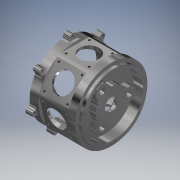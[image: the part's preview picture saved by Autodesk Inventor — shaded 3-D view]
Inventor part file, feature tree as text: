
AUTODESK INVENTOR PART (.ipt)
format: ipt  version: 2018 (Build 220112000, 112)  size: 513,024 bytes
history: native  units: mm
features: sketch x10, extrude x10, hole x4, pattern_circular x2, direct_edit x1, chamfer x1, other x1, revolve x1, projected_geometry x1
ambient origin geometry x8: Origin, YZ Plane, XZ Plane, XY Plane, X Axis, Y Axis, Z Axis, Center Point
bodies: Solid1 (feature_tree)
feature tree (31):
  sketch  "Sketch1"  dims[d0=100.0mm d1=90.0mm]
  extrude  "Extrusion1"  Depth=90.0mm
  extrude  "Extrusion2"  Depth=67.0mm TaperAngle=0.0deg
  extrude  "Extrusion3"  Depth=4.07mm
  extrude  "Extrusion4"  Depth=13.0mm TaperAngle=0.0deg
  extrude  "Extrusion5"  Depth=18.0mm
  direct_edit  "Direct Edit1"
  extrude  "Extrusion6"  Depth=12.0mm
  extrude  "Extrusion7"  Depth=30.0mm TaperAngle=360.0deg
  chamfer  "Chamfer1"  Distance=9.0mm
  extrude  "Extrusion8"  Depth=10.0mm
  sketch  "Sketch8"  dims[d28=8.0mm d29=30.0mm d31=360.0deg]
  extrude  "Extrusion9"  Depth=10.0mm TaperAngle=0.0deg
  hole  "Hole1"  [1 undecoded]
  extrude  "Extrusion10"  Depth=10.0mm TaperAngle=0.0deg
  hole  "Hole2"  [1 undecoded]
  hole  "Hole3"  [1 undecoded]
  other  "Work Axis1"
  pattern_circular  "Circular Pattern1"  [2 undecoded]
  hole  "Hole4"  [1 undecoded]
  pattern_circular  "Circular Pattern2"  [2 undecoded]
  sketch  "Sketch2"  dims[d2=80.0mm d3=67.0mm d4=0.0mm]
  sketch  "Sketch4"  dims[d5=4.07mm d6=0.0mm d7=85.0mm]
  sketch  "Sketch5"  dims[d8=50.0mm d9=0.0mm d10=13.0mm d11=0.0mm]
  sketch  "Sketch6"  dims[d12=43.0mm d22=21.5mm d25=18.0mm]
  sketch  "Sketch7"  dims[d26=25.0mm d27=12.0mm]
  sketch  "Sketch9"  dims[d33=21.5mm]
  sketch  "Sketch10"  dims[d34=21.5mm d35=9.0mm d36=0.0mm]
  sketch  "Sketch11"  dims[d37=-15.707963mm d38=35.0mm d39=10.0mm d40=0.0mm d41=17.35mm d42=17.0mm d43=0.0mm d44=2.0mm d45=2.0mm d46=45.0deg d47=40.0mm d48=10.43mm d49=46.0mm d50=39.19mm d51=0.0mm d53=39.19mm d54=0.0mm d55=27.0mm d57=19.595mm d58=32.0mm d59=32.0mm d60=3.242mm d61=8.0mm d62=3.023mm d63=2.0mm d64=14.3117mm d65=11.8mm d66=20.594885mm d67=20.0mm d68=114.55mm d69=8.0mm d70=9.0mm d71=0.0mm d72=10.0mm d73=10.0mm d74=4.134mm d75=10.0mm d76=3.023mm d77=2.0mm d78=14.3117mm d79=14.2mm d80=20.594885mm d81=46.0mm d82=3.242mm d83=8.0mm d84=3.023mm d85=2.0mm d86=14.3117mm d87=10.8mm d88=20.594885mm d89=70.0mm d90=360.0deg d92=85.0mm d93=3.242mm d94=8.0mm d95=3.023mm d96=2.0mm d97=14.3117mm d98=13.3mm d99=20.594885mm d100=70.0mm d101=360.0deg]
  revolve  "Rotate1"  [1 undecoded]
  projected_geometry  "Project Cut Edges1"
note: 9 required parameter values undecoded (feature->parameter linkage not recoverable at this tier; creation-order binding heuristic only, values carry confidence <= 0.55)